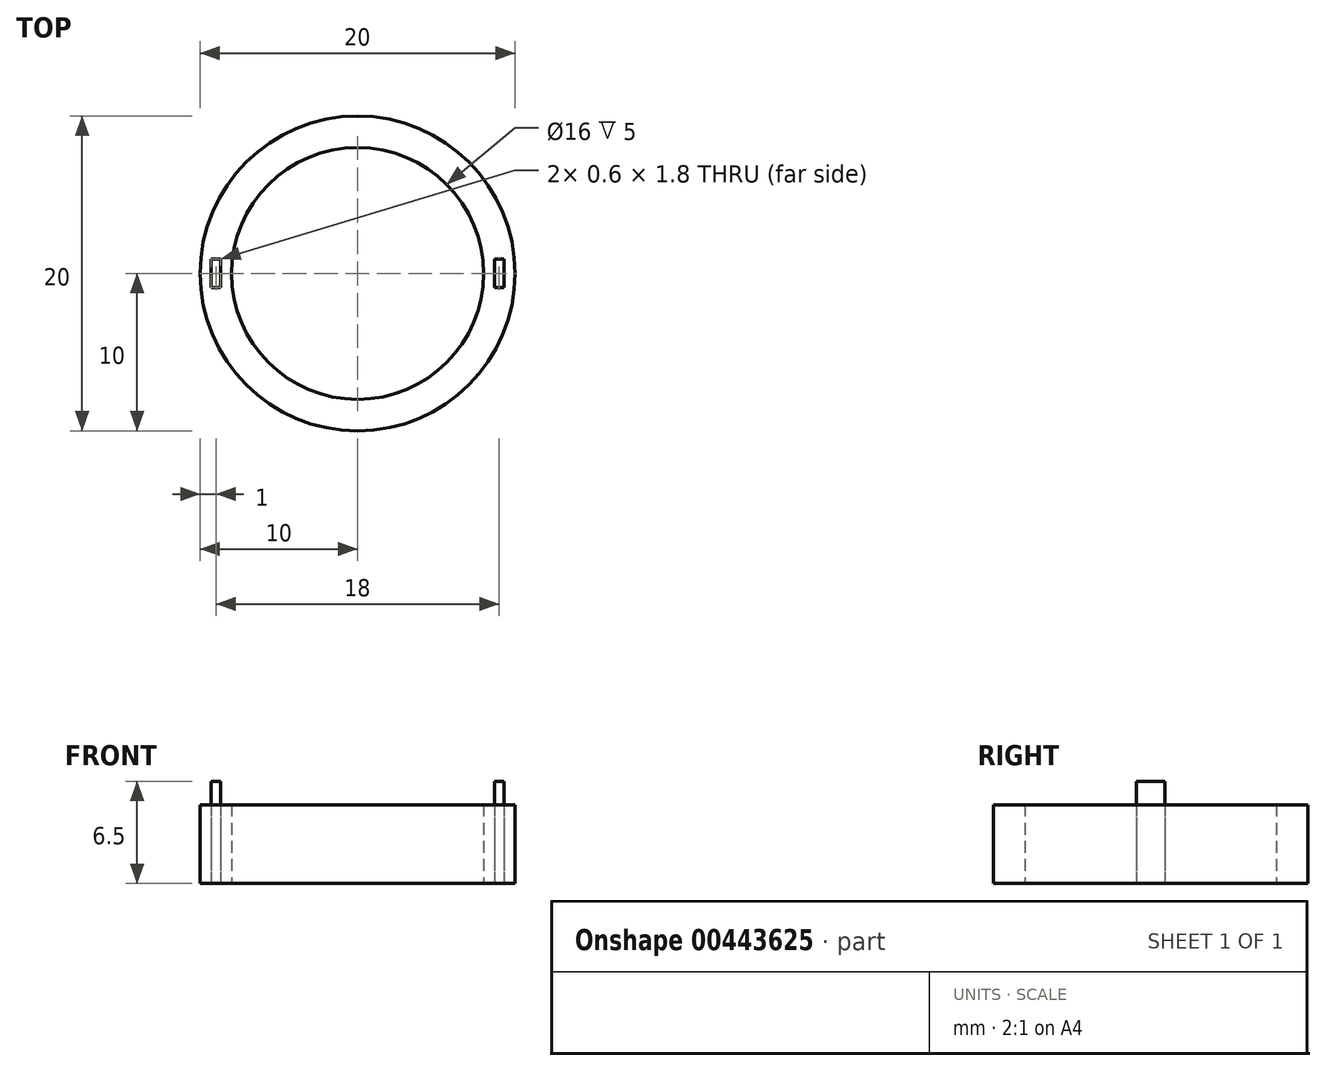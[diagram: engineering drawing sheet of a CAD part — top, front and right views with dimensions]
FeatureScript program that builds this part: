
annotation { "Feature Type Name" : "Feature", "Feature Type Description" : "" }
export const myFeature = defineFeature(function(context is Context, id is Id, definition is map)
    precondition{}
    {
        {
            var Q0;
            Q0=qCreatedBy(makeId("Top.planeOp"),FACE);
            var sketch = newSketch(context, id + "F0", { "sketchPlane" : qUnion([Q0])});
            skCircle(sketch, "E0", {"center": v(0, 0) * mm, "radius": 10 * mm});
            skCircle(sketch, "E1", {"center": v(0, 0) * mm, "radius": 8 * mm});
            skLineSegment(sketch, "E2.bottom", {"start": v(-9.3, 0.9) * mm, "end": v(-8.7, 0.9) * mm});
            skLineSegment(sketch, "E2.top", {"start": v(-9.3, -0.9) * mm, "end": v(-8.7, -0.9) * mm});
            skLineSegment(sketch, "E2.left", {"start": v(-9.3, 0.9) * mm, "end": v(-9.3, -0.9) * mm});
            skLineSegment(sketch, "E2.right", {"start": v(-8.7, 0.9) * mm, "end": v(-8.7, -0.9) * mm});
            skLineSegment(sketch, "E3.bottom", {"start": v(8.7, 0.9) * mm, "end": v(9.3, 0.9) * mm});
            skLineSegment(sketch, "E3.top", {"start": v(8.7, -0.9) * mm, "end": v(9.3, -0.9) * mm});
            skLineSegment(sketch, "E3.left", {"start": v(8.7, 0.9) * mm, "end": v(8.7, -0.9) * mm});
            skLineSegment(sketch, "E3.right", {"start": v(9.3, 0.9) * mm, "end": v(9.3, -0.9) * mm});
            skSolve(sketch);
        }
        {
            var Q0;
            Q0=makeQuery(id+"F0.imprint","IMPRINT",FACE,{"disambiguationData":[TD([[makeQuery(id+"F0.imprint","IMPRINT",EDGE,{"derivedFrom":sQuery(id+"F0.wireOp",EDGE,"E2.bottom")}),-1.0]])]});
            var Q1;
            Q1=makeQuery(id+"F0.imprint","IMPRINT",FACE,{"disambiguationData":[TD([[makeQuery(id+"F0.imprint","IMPRINT",EDGE,{"derivedFrom":sQuery(id+"F0.wireOp",EDGE,"E3.bottom")}),-1.0]])]});
            extrude(context, id + "F1", {"entities" : qUnion([Q0, Q1]), "depth" : 6.5 * mm});
        }
        {
            var Q0;
            Q0 = qSketchRegion(id + "F0", true);
            extrude(context, id + "F2", {"entities" : qUnion([Q0]), "depth" : 5 * mm});
        }
    });
